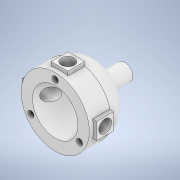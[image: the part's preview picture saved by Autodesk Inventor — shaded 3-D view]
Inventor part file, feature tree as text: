
AUTODESK INVENTOR PART (.ipt)
format: ipt  version: 2020 (Build 240168000, 168)  size: 283,136 bytes
history: native  units: mm
features: extrude x7, sketch x6, plane x4, fillet x1, other x1, pattern_circular x1
ambient origin geometry x8: Origin, YZ Plane, XZ Plane, XY Plane, X Axis, Y Axis, Z Axis, Center Point
bodies: Solid1 (feature_tree)
feature tree (20):
  extrude  "Base"  Depth=17.5mm TaperAngle=0.0deg
  plane  "Work Plane1"
  extrude  "IR hole"  TaperAngle=0.0deg  [1 undecoded]
  plane  "Work Plane2"
  extrude  "LED Hole"  Depth=13.5mm TaperAngle=0.0deg
  extrude  "Water Tube wall"  Depth=10.0mm TaperAngle=0.0deg
  fillet  "Fillet1"  Radius=5.0mm
  plane  "Work Plane3"
  other  "Inner cut out"
  extrude  "Mount screw holes"  Depth=9.0mm
  plane  "Work Plane4"
  extrude  "Hole wall"  Depth=4.5mm
  pattern_circular  "Circular Pattern1"  Angle=90.0deg  [1 undecoded]
  extrude  "Extrusion12"  Depth=6.6mm
  sketch  "Sketch2"  dims[d0=27.0mm d1=17.5mm d2=0.0mm]
  sketch  "Sketch7"  dims[d4=5.1mm d5=0.0mm d6=0.0mm]
  sketch  "Sketch13"  dims[d7=5.1mm d8=13.5mm d9=0.0mm]
  sketch  "Sketch14"  dims[d24=2.5mm d26=10.0mm d27=0.0mm d31=5.0mm]
  sketch  "Sketch15"  dims[d32=5.0mm d35=9.0mm]
  sketch  "Sketch17"  dims[d39=2.0mm d40=4.5mm d41=90.0deg d42=2.5mm d43=2.4mm d44=4.5mm d45=30.0mm d47=360.0deg d49=5.0mm d50=0.0mm d51=-1.0mm d52=5.0mm d53=5.1mm d54=6.6mm d55=6.6mm d56=2.25mm d57=0.0mm d58=30.0mm d59=180.0deg d64=20.0mm d65=0.0mm d66=18.0mm d67=22.2mm d68=2.5mm d22=0.5mm d23=0.872665mm d25=0.872665mm d33=0.5mm d34=0.872665mm d36=0.872665mm d61=0.5mm d62=0.872665mm d63=0.5mm]
note: 2 required parameter values undecoded (feature->parameter linkage not recoverable at this tier; creation-order binding heuristic only, values carry confidence <= 0.55)
